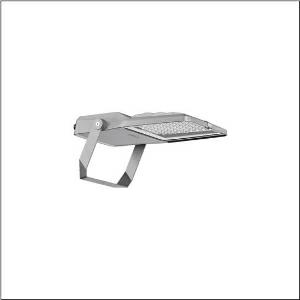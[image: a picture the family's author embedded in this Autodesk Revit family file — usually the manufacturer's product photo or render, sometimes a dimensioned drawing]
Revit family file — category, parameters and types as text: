
# Revit family: floodlight_fl_21_iq_mini___pl52_5xa7771b2d1a_9873
name_source: partatom
category: Lighting Fixtures
units: mm (PartAtom-declared; Revit-internal decimal feet)

## family parameters
Cut with Voids When Loaded = No
Host = Face
Light Source = No
Part Type = Normal
Room Calculation Point = No
Round Connector Dimension = Use Diameter
Shared = No

## types (1)
- --- (1 x LED, 6240 lm, 45.5 W, 3000K)
    Apparent Load = 46 VA
    CIE Flux Codes = 26 60 98 100 100
    Color Rendering = 70
    Color Temperature = 3000K
    Default Elevation = 1800 mm
    Description = Floodlight FL 21 iQ mini, floodlight, primary light control with lens, of PMMA, primary optical cover: protective disc, of toughened safety glass, transparent, light distribution: PL52, light emission: direct distribution, installation type: surface-mounted, LED, High Power LED, rated luminous flux: 6.240lm, luminous efficacy: 137lm/W, light colour: 730, colour temperature: 3000K, control gear: iQ Comfort/DALI, control: Auto-Match, Temp-Guard, Lumen-Switch, Night-Set, Smart-Wire, Light-Fading, Desk-Remote (wireless, voltage-free reading and setting of iQ features in the workshop via application-optimized NFC function/RFID function), optimised constant luminous flux control (CLO 2.0), with terminal, 6-pole, mains connection: 220..240V, AC, 50/60Hz, start of lifetime: 46W, end of service life: 48W, reduction: 22W, luminaire housing, of diecast aluminium, powder-coated, Siteco® metallic grey (DB 702S), corrosivity category C5 mid according to DIN EN ISO 12944, suitable for swimming pools, chlorine-resistant, sealing non-destructively replaceable, mounting bracket, of steel, galvanised, powder-coated, Siteco® metallic grey (DB 702S), protection rating (complete): IP66, insulation class (complete): insulation class II (safety insulation), certification: CE, ENEC, VDE, protection symbol: D, impact resistance: IK08, permissible operating ambient temperature: -40..+40°C, permissible operating ambient temperature for outdoor applications: -40..+50°C, standard: DIN EN 12944, LABS conformity tested according to VDMA 24364:2018-05, packaging unit: 1 piece

Light Distribution: PL52
    Height = 70 mm
    Lamp = 1 x LED
    Lamp Light Flux = 6240 lm
    Lamp Power = 45.5 W
    Lamp count = 1
    Length = 485 mm
    Luminous efficacy = 137 lm/W
    Manufacturer = Siteco
    ModVariant = No
    Model = 5XA7771B2D1A
    Mounting Place = Wall
    Mounting Type = Surface mounted
    Number of Poles = 1
    OnlyDefault = Yes
    Power Factor = 1
    Product Name = Floodlight FL 21 iQ mini | PL52
    Product group = floodlight | wall mounted
    ProductGroupID = 2001
    Protection Class = Protection class II
    Protection Degree = IP 66
    RLX_Detail_Level = 1
    RLX_Emergency_Light_Flux = 0 lm
    RLX_Emergency_Type = 0
    RLX_Emergency_Type_DB = No
    RlxData = <blob elided: 96389 chars, md5=79c57c2a>
    Socket = socket
    Standby Power = 0 W
    System Light Flux = 6240 lm
    System Power = 46 W
    Type Comments = factory setting: luminous flux: 100 % | dim-lin: 254 | 463 mA
    Type Image = l_1006845.jpg
    URL = http://relux.com
    VarID = @adj_165168
    Voltage = 0 V
    Weight = 0.00 kg
    Width = 337 mm

## geometry (parser evidence)
native form markers: Blend x4, Sweep x13
no freeform markers — native parametric forms only
